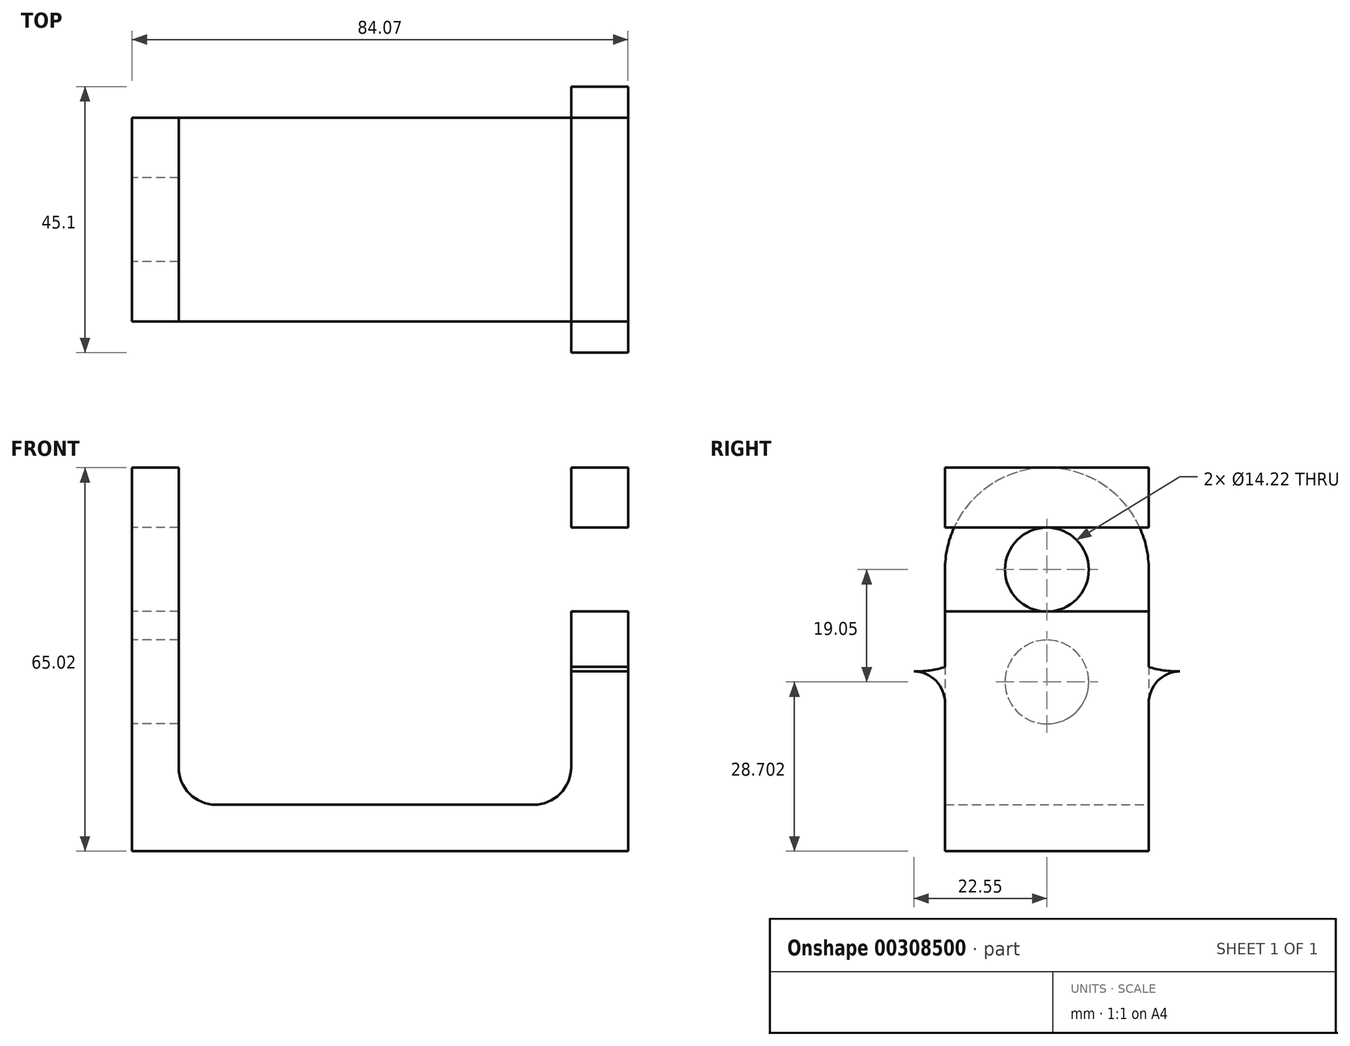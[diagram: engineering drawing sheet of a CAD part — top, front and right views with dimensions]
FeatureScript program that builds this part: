
annotation { "Feature Type Name" : "Feature", "Feature Type Description" : "" }
export const myFeature = defineFeature(function(context is Context, id is Id, definition is map)
    precondition{}
    {
        {
            var Q0;
            Q0=qCreatedBy(makeId("Front.planeOp"),FACE);
            var sketch = newSketch(context, id + "F0", { "sketchPlane" : qUnion([Q0])});
            skLineSegment(sketch, "E0", {"start": v(0, 0) * mm, "end": v(0, 65.02) * mm});
            skLineSegment(sketch, "E1", {"start": v(0, 65.02) * mm, "end": v(7.87, 65.02) * mm});
            skLineSegment(sketch, "E2", {"start": v(7.87, 65.02) * mm, "end": v(7.87, 7.87) * mm});
            skLineSegment(sketch, "E3", {"start": v(7.87, 7.87) * mm, "end": v(74.42, 7.87) * mm});
            skLineSegment(sketch, "E4", {"start": v(74.42, 7.87) * mm, "end": v(74.42, 65.02) * mm});
            skLineSegment(sketch, "E5", {"start": v(74.42, 65.02) * mm, "end": v(84.07, 65.02) * mm});
            skLineSegment(sketch, "E6", {"start": v(84.07, 65.02) * mm, "end": v(84.07, 0) * mm});
            skLineSegment(sketch, "E7", {"start": v(84.07, 0) * mm, "end": v(0, 0) * mm});
            skArc(sketch, "E8", {"start": v(7.87, 14.22) * mm, "mid": v(9.73, 9.73) * mm, "end": v(14.22, 7.87) * mm});
            skArc(sketch, "E9", {"start": v(68.07, 7.87) * mm, "mid": v(72.56, 9.73) * mm, "end": v(74.42, 14.22) * mm});
            skSolve(sketch);
        }
        {
            var Q0;
            {var subQ3=sQuery(id+"F0.wireOp",EDGE,"E8");Q0=makeQuery(id+"F0.imprint","IMPRINT",FACE,{"disambiguationData":[TD([[makeQuery(id+"F0.imprint","IMPRINT",EDGE,{"derivedFrom":subQ3}),-1.0]])]});}
            var Q1;
            {var subQ3=sQuery(id+"F0.wireOp",EDGE,"E9");Q1=makeQuery(id+"F0.imprint","IMPRINT",FACE,{"disambiguationData":[TD([[makeQuery(id+"F0.imprint","IMPRINT",EDGE,{"derivedFrom":subQ3}),-1.0]])]});}
            var Q2;
            Q2=makeQuery(id+"F0.imprint","IMPRINT",FACE,{"disambiguationData":[TD([[makeQuery(id+"F0.imprint","IMPRINT",EDGE,{"derivedFrom":sQuery(id+"F0.wireOp",EDGE,"E0")}),-1.0]])]});
            extrude(context, id + "F1", {"entities" : qUnion([Q0, Q1, Q2]), "endBound" : BoundingType.SYMMETRIC, "depth" : 34.54 * mm});
        }
        {
            var Q0;
            Q0=makeQuery(id+"F1.opExtrude","SWEPT_FACE",FACE,{"disambiguationData":[OSD([sQuery(id+"F0.wireOp",EDGE,"E0")])]});
            var sketch = newSketch(context, id + "F2", { "sketchPlane" : qUnion([Q0])});
            skLineSegment(sketch, "E10", {"start": v(0, 0) * mm, "end": v(0, 65.02) * mm, "construction": true});
            skLineSegment(sketch, "E11", {"start": v(-17.27, 47.75) * mm, "end": v(17.27, 47.75) * mm, "construction": true});
            skLineSegment(sketch, "E12", {"start": v(17.27, 28.7) * mm, "end": v(-17.27, 28.7) * mm, "construction": true});
            skArc(sketch, "E13", {"start": v(17.27, 47.75) * mm, "mid": v(0, 65.02) * mm, "end": v(-17.27, 47.75) * mm});
            skCircle(sketch, "E14", {"center": v(0, 47.75) * mm, "radius": 7.11 * mm});
            skCircle(sketch, "E15", {"center": v(0, 28.7) * mm, "radius": 7.11 * mm});
            skSolve(sketch);
        }
        {
            var Q0;
            {var subQ0=sQuery(id+"F2.wireOp",EDGE,"E13");var subQ1=sQuery(id+"F0.wireOp",EDGE,"E0");var subQ2=makeQuery(id+"F1.opExtrude","CAP_EDGE",EDGE,{"disambiguationData":[OSD([subQ1])],"isStart":true});var subQ3=makeQuery(id+"F2.imprint","INTERSECT",VERTEX,{"derivedFrom":[subQ2,subQ0]});Q0=makeQuery(id+"F2.imprint","IMPRINT",FACE,{"disambiguationData":[TD([[makeQuery(id+"F2.imprint","IMPRINT",EDGE,{"disambiguationData":[TD([[subQ3,1.0]])],"derivedFrom":subQ0}),-1.0]])]});}
            var Q1;
            {var subQ0=sQuery(id+"F2.wireOp",EDGE,"E13");var subQ1=sQuery(id+"F0.wireOp",EDGE,"E0");var subQ2=makeQuery(id+"F1.opExtrude","CAP_EDGE",EDGE,{"disambiguationData":[OSD([subQ1])],"isStart":false});var subQ3=makeQuery(id+"F2.imprint","INTERSECT",VERTEX,{"derivedFrom":[subQ2,subQ0]});Q1=makeQuery(id+"F2.imprint","IMPRINT",FACE,{"disambiguationData":[TD([[makeQuery(id+"F2.imprint","IMPRINT",EDGE,{"disambiguationData":[TD([[subQ3,-1.0]])],"derivedFrom":subQ0}),-1.0]])]});}
            var Q2;
            Q2=makeQuery(id+"F2.imprint","IMPRINT",FACE,{"disambiguationData":[TD([[makeQuery(id+"F2.imprint","IMPRINT",EDGE,{"derivedFrom":sQuery(id+"F2.wireOp",EDGE,"E14")}),1.0]])]});
            var Q3;
            Q3=makeQuery(id+"F2.imprint","IMPRINT",FACE,{"disambiguationData":[TD([[makeQuery(id+"F2.imprint","IMPRINT",EDGE,{"derivedFrom":sQuery(id+"F2.wireOp",EDGE,"E15")}),1.0]])]});
            var Q4;
            Q4=makeQuery(id+"F1.opExtrude","SWEPT_FACE",FACE,{"disambiguationData":[OSD([sQuery(id+"F0.wireOp",EDGE,"E2")])]});
            extrude(context, id + "F3", {"entities" : qUnion([Q0, Q1, Q2, Q3]), "operationType" : NewBodyOperationType.REMOVE, "endBound" : BoundingType.UP_TO_SURFACE, "oppositeDirection" : true, "endBoundEntityFace" : qUnion([Q4]), "depth" : 25.4 * mm});
        }
        {
            var Q0;
            Q0=makeQuery(id+"F1.opExtrude","SWEPT_FACE",FACE,{"disambiguationData":[OSD([sQuery(id+"F0.wireOp",EDGE,"E6")])]});
            var sketch = newSketch(context, id + "F4", { "sketchPlane" : qUnion([Q0])});
            skLineSegment(sketch, "E16", {"start": v(-73.36, 47.75) * mm, "end": v(73.7, 47.75) * mm, "construction": true});
            skLineSegment(sketch, "E17", {"start": v(-22.35, 54.86) * mm, "end": v(-22.35, 40.64) * mm, "construction": true});
            skLineSegment(sketch, "E18", {"start": v(22.35, 54.86) * mm, "end": v(22.35, 40.64) * mm, "construction": true});
            skLineSegment(sketch, "E19", {"start": v(0, 0) * mm, "end": v(0, 65.02) * mm, "construction": true});
            skArc(sketch, "E20", {"start": v(-22.35, 54.86) * mm, "mid": v(-29.46, 47.75) * mm, "end": v(-22.35, 40.64) * mm});
            skArc(sketch, "E21", {"start": v(22.35, 40.64) * mm, "mid": v(29.46, 47.75) * mm, "end": v(22.35, 54.86) * mm});
            skLineSegment(sketch, "E22", {"start": v(-22.35, 54.86) * mm, "end": v(22.35, 54.86) * mm});
            skLineSegment(sketch, "E23", {"start": v(22.35, 40.64) * mm, "end": v(-22.35, 40.64) * mm});
            skLineSegment(sketch, "E24.bottom", {"start": v(-17.27, 0) * mm, "end": v(17.27, 0) * mm, "construction": true});
            skLineSegment(sketch, "E24.left", {"start": v(-17.27, 0) * mm, "end": v(-17.27, 65.02) * mm, "construction": true});
            skLineSegment(sketch, "E25", {"start": v(-17.27, 21.85) * mm, "end": v(-17.27, 40.64) * mm});
            skLineSegment(sketch, "E26", {"start": v(17.27, 21.85) * mm, "end": v(17.27, 40.64) * mm});
            skLineSegment(sketch, "E27", {"start": v(-17.27, 21.85) * mm, "end": v(-17.27, 25.56) * mm});
            skLineSegment(sketch, "E28", {"start": v(17.27, 30.48) * mm, "end": v(17.27, 21.85) * mm});
            skArc(sketch, "E29", {"start": v(-30.9, 62.76) * mm, "mid": v(-38.2, 40.9) * mm, "end": v(-17.27, 31.24) * mm});
            skArc(sketch, "E30", {"start": v(17.27, 31.24) * mm, "mid": v(38.82, 42.53) * mm, "end": v(27.7, 64.17) * mm});
            skLineSegment(sketch, "E31", {"start": v(-22.35, 65.02) * mm, "end": v(22.35, 65.02) * mm});
            skArc(sketch, "E32", {"start": v(-17.27, 25.15) * mm, "mid": v(-18.81, 28.9) * mm, "end": v(-22.55, 30.48) * mm});
            skArc(sketch, "E33", {"start": v(22.55, 30.48) * mm, "mid": v(18.81, 28.9) * mm, "end": v(17.27, 25.15) * mm});
            skLineSegment(sketch, "E34", {"start": v(-17.27, 31.24) * mm, "end": v(-17.27, 25.56) * mm});
            skLineSegment(sketch, "E35", {"start": v(17.27, 31.24) * mm, "end": v(17.27, 25.15) * mm});
            skSolve(sketch);
        }
        {
            var Q0;
            {var subQ6=sQuery(id+"F4.wireOp",EDGE,"E20");Q0=makeQuery(id+"F4.imprint","IMPRINT",FACE,{"disambiguationData":[TD([[makeQuery(id+"F4.imprint","IMPRINT",EDGE,{"derivedFrom":subQ6}),-1.0]])]});}
            var Q1;
            {var subQ2=sQuery(id+"F4.wireOp",EDGE,"8e83Uar0-yaf4-wzII-FnTj-t0QCjeUICcAs");Q1=makeQuery(id+"F4.imprint","IMPRINT",FACE,{"disambiguationData":[TD([[makeQuery(id+"F4.imprint","IMPRINT",EDGE,{"derivedFrom":subQ2}),-1.0]])]});}
            var Q2;
            {var subQ2=sQuery(id+"F4.wireOp",EDGE,"cvOcdRIy-CgPM-bboW-LZQl-oUqmpzIFxoTf");Q2=makeQuery(id+"F4.imprint","IMPRINT",FACE,{"disambiguationData":[TD([[makeQuery(id+"F4.imprint","IMPRINT",EDGE,{"derivedFrom":subQ2}),-1.0]])]});}
            var Q3;
            {var subQ8=sQuery(id+"F4.wireOp",EDGE,"E21");Q3=makeQuery(id+"F4.imprint","IMPRINT",FACE,{"disambiguationData":[TD([[makeQuery(id+"F4.imprint","IMPRINT",EDGE,{"derivedFrom":subQ8}),-1.0]])]});}
            var Q4;
            {var subQ3=sQuery(id+"F4.wireOp",EDGE,"E33");Q4=makeQuery(id+"F4.imprint","IMPRINT",FACE,{"disambiguationData":[TD([[makeQuery(id+"F4.imprint","IMPRINT",EDGE,{"derivedFrom":subQ3}),-1.0]])]});}
            var Q5;
            {var subQ2=sQuery(id+"F4.wireOp",EDGE,"E32");Q5=makeQuery(id+"F4.imprint","IMPRINT",FACE,{"disambiguationData":[TD([[makeQuery(id+"F4.imprint","IMPRINT",EDGE,{"derivedFrom":subQ2}),-1.0]])]});}
            var Q6;
            {var subQ0=sQuery(id+"F4.wireOp",EDGE,"E30");var subQ1=makeQuery(id+"F1.opExtrude","CAP_EDGE",EDGE,{"disambiguationData":[OSD([sQuery(id+"F0.wireOp",EDGE,"E6")])],"isStart":true});var subQ2=makeQuery(id+"F4.imprint","INTERSECT",VERTEX,{"derivedFrom":[subQ1,subQ0]});Q6=makeQuery(id+"F4.imprint","IMPRINT",FACE,{"disambiguationData":[TD([[makeQuery(id+"F4.imprint","IMPRINT",EDGE,{"disambiguationData":[TD([[subQ2,1.0]])],"derivedFrom":subQ0}),-1.0]])]});}
            var Q7;
            {var subQ0=sQuery(id+"F4.wireOp",EDGE,"E29");var subQ1=makeQuery(id+"F1.opExtrude","CAP_EDGE",EDGE,{"disambiguationData":[OSD([sQuery(id+"F0.wireOp",EDGE,"E6")])],"isStart":false});var subQ2=makeQuery(id+"F4.imprint","INTERSECT",VERTEX,{"derivedFrom":[subQ1,subQ0]});Q7=makeQuery(id+"F4.imprint","IMPRINT",FACE,{"disambiguationData":[TD([[makeQuery(id+"F4.imprint","IMPRINT",EDGE,{"disambiguationData":[TD([[subQ2,-1.0]])],"derivedFrom":subQ0}),-1.0]])]});}
            var Q8;
            Q8=makeQuery(id+"F1.opExtrude","SWEPT_FACE",FACE,{"disambiguationData":[OSD([sQuery(id+"F0.wireOp",EDGE,"E4")])]});
            extrude(context, id + "F5", {"entities" : qUnion([Q0, Q1, Q2, Q3, Q4, Q5, Q6, Q7]), "operationType" : NewBodyOperationType.ADD, "endBound" : BoundingType.UP_TO_SURFACE, "oppositeDirection" : true, "endBoundEntityFace" : qUnion([Q8]), "depth" : 25.4 * mm});
        }
        {
            var Q0;
            {var subQ0=sQuery(id+"F4.wireOp",EDGE,"E22");var subQ1=sQuery(id+"F0.wireOp",EDGE,"E6");var subQ2=makeQuery(id+"F1.opExtrude","CAP_EDGE",EDGE,{"disambiguationData":[OSD([subQ1])],"isStart":false});var subQ3=makeQuery(id+"F4.imprint","INTERSECT",VERTEX,{"derivedFrom":[subQ2,subQ0]});Q0=makeQuery(id+"F4.imprint","IMPRINT",FACE,{"disambiguationData":[TD([[makeQuery(id+"F4.imprint","IMPRINT",EDGE,{"disambiguationData":[TD([[subQ3,-1.0]])],"derivedFrom":subQ0}),-1.0]])]});}
            var Q1;
            {var subQ0=sQuery(id+"F4.wireOp",EDGE,"E23");var subQ1=sQuery(id+"F4.wireOp",EDGE,"E22");var subQ2=sQuery(id+"F0.wireOp",EDGE,"E6");var subQ3=sQuery(id+"F0.wireOp",EDGE,"E4");Q1=makeQuery(id+"F5.boolean.opBoolean","MERGE",FACE,{"derivedFrom":[makeQuery(id+"F1.opExtrude","SWEPT_FACE",FACE,{"disambiguationData":[OSD([subQ3])]}),makeQuery(id+"F5.opExtrude","CAP_FACE",FACE,{"disambiguationData":[OSD([subQ3]),ownerDisambiguation([makeQuery(id+"F5.opExtrude","SWEPT_BODY",BODY,{"disambiguationData":[OSD([subQ2,sQuery(id+"F4.wireOp",EDGE,"E20"),subQ1,subQ0,sQuery(id+"F4.wireOp",EDGE,"fd3767ad-614c-4b6a-b884-39be4fc57cb1"),sQuery(id+"F4.wireOp",EDGE,"8e83Uar0-yaf4-wzII-FnTj-t0QCjeUICcAs"),sQuery(id+"F4.wireOp",EDGE,"E25"),sQuery(id+"F4.wireOp",EDGE,"E27")])]})])],"isStart":false}),makeQuery(id+"F5.opExtrude","CAP_FACE",FACE,{"disambiguationData":[OSD([subQ3]),ownerDisambiguation([makeQuery(id+"F5.opExtrude","SWEPT_BODY",BODY,{"disambiguationData":[OSD([subQ2,sQuery(id+"F4.wireOp",EDGE,"E21"),subQ1,subQ0,sQuery(id+"F4.wireOp",EDGE,"8f62399c-c58d-42b0-9eed-b89b524e638a"),sQuery(id+"F4.wireOp",EDGE,"cvOcdRIy-CgPM-bboW-LZQl-oUqmpzIFxoTf"),sQuery(id+"F4.wireOp",EDGE,"E26"),sQuery(id+"F4.wireOp",EDGE,"E28")])]})])],"isStart":false})]});}
            extrude(context, id + "F6", {"entities" : qUnion([Q0]), "operationType" : NewBodyOperationType.REMOVE, "endBound" : BoundingType.UP_TO_SURFACE, "oppositeDirection" : true, "endBoundEntityFace" : qUnion([Q1]), "depth" : 25.4 * mm});
        }
    });
